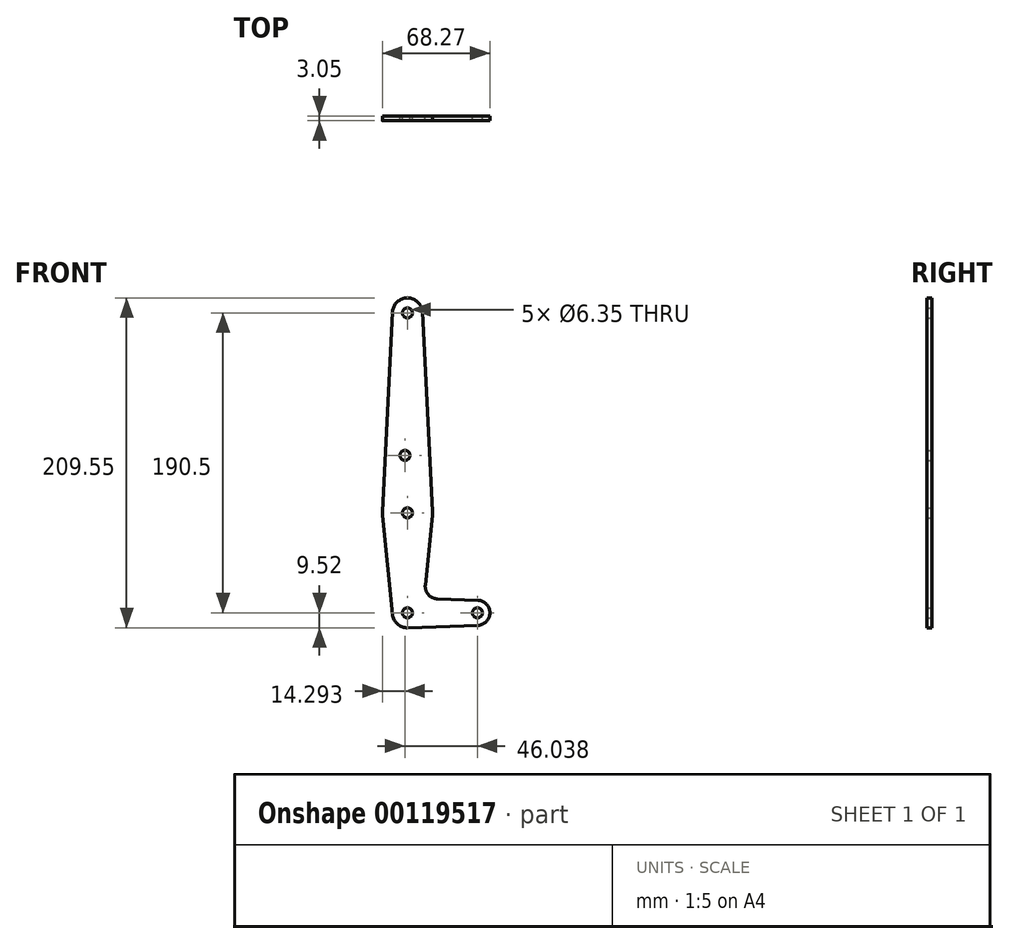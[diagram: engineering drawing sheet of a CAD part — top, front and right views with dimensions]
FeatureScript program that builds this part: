
annotation { "Feature Type Name" : "Feature", "Feature Type Description" : "" }
export const myFeature = defineFeature(function(context is Context, id is Id, definition is map)
    precondition{}
    {
        {
            var Q0;
            Q0=qCreatedBy(makeId("Front.planeOp"),FACE);
            var sketch = newSketch(context, id + "F0", { "sketchPlane" : qUnion([Q0])});
            skCircle(sketch, "E0", {"center": v(0, 0) * mm, "radius": 9.53 * mm});
            skCircle(sketch, "E1", {"center": v(0, 63.5) * mm, "radius": 15.88 * mm});
            skCircle(sketch, "E2", {"center": v(44.45, 0) * mm, "radius": 7.94 * mm});
            skCircle(sketch, "E3", {"center": v(0, 190.5) * mm, "radius": 9.53 * mm});
            skCircle(sketch, "E4", {"center": v(0, 190.5) * mm, "radius": 3.18 * mm});
            skLineSegment(sketch, "E5", {"start": v(0, 190.5) * mm, "end": v(0, 0) * mm, "construction": true});
            skLineSegment(sketch, "E6", {"start": v(44.45, 0) * mm, "end": v(0, 0) * mm, "construction": true});
            skLineSegment(sketch, "E7", {"start": v(-9.51, 190.98) * mm, "end": v(-15.86, 64.3) * mm});
            skLineSegment(sketch, "E8", {"start": v(9.51, 190.98) * mm, "end": v(15.86, 64.3) * mm});
            skLineSegment(sketch, "E9", {"start": v(-15.8, 61.91) * mm, "end": v(-9.48, -0.95) * mm});
            skLineSegment(sketch, "E10", {"start": v(15.8, 61.91) * mm, "end": v(11.34, 17.6) * mm});
            skLineSegment(sketch, "E11", {"start": v(0.34, -9.52) * mm, "end": v(44.73, -7.93) * mm});
            skLineSegment(sketch, "E12", {"start": v(18.97, 8.85) * mm, "end": v(44.73, 7.93) * mm});
            skCircle(sketch, "E13", {"center": v(-1.59, 100.03) * mm, "radius": 3.18 * mm});
            skCircle(sketch, "E14", {"center": v(0, 63.5) * mm, "radius": 3.18 * mm});
            skCircle(sketch, "E15", {"center": v(0, 0) * mm, "radius": 3.18 * mm});
            skCircle(sketch, "E16", {"center": v(44.45, 0) * mm, "radius": 3.18 * mm});
            skArc(sketch, "E17.filletArc", {"start": v(11.34, 17.6) * mm, "mid": v(13.26, 11.57) * mm, "end": v(18.97, 8.85) * mm});
            skSolve(sketch);
        }
        {
            var Q0;
            Q0 = qSketchRegion(id + "F0", true);
            extrude(context, id + "F1", {"entities" : qUnion([Q0]), "depth" : 3.05 * mm});
        }
    });
